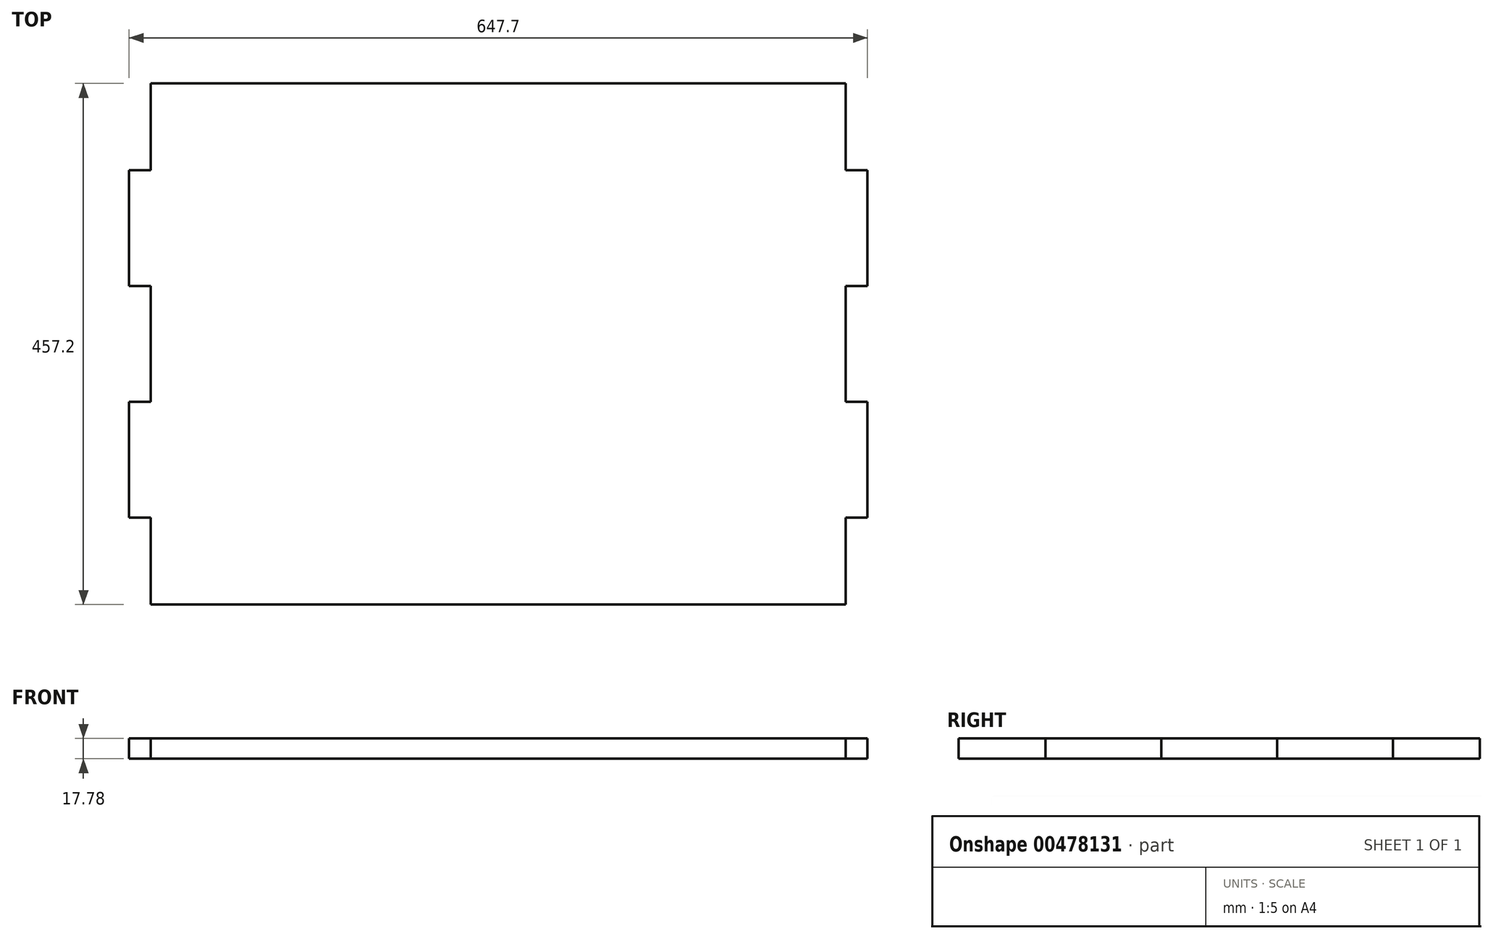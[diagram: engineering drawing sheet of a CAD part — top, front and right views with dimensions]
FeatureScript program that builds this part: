
annotation { "Feature Type Name" : "Feature", "Feature Type Description" : "" }
export const myFeature = defineFeature(function(context is Context, id is Id, definition is map)
    precondition{}
    {
        {
            var Q0;
            Q0=qCreatedBy(makeId("Top.planeOp"),FACE);
            var sketch = newSketch(context, id + "F0", { "sketchPlane" : qUnion([Q0])});
            skLineSegment(sketch, "E0.bottom", {"start": v(0, 0) * mm, "end": v(609.6, 0) * mm});
            skLineSegment(sketch, "E0.top", {"start": v(0, -457.2) * mm, "end": v(609.6, -457.2) * mm});
            skLineSegment(sketch, "E1.0", {"start": v(628.65, 0) * mm, "end": v(628.65, -457.2) * mm, "construction": true});
            skLineSegment(sketch, "E2.0", {"start": v(-19.05, 0) * mm, "end": v(-19.05, -457.2) * mm, "construction": true});
            skLineSegment(sketch, "E3.0", {"start": v(0, -76.2) * mm, "end": v(609.6, -76.2) * mm});
            skLineSegment(sketch, "E4.0", {"start": v(0, -381) * mm, "end": v(609.6, -381) * mm});
            skLineSegment(sketch, "E5.0", {"start": v(0, -279.4) * mm, "end": v(609.6, -279.4) * mm});
            skLineSegment(sketch, "E6.0", {"start": v(0, -177.8) * mm, "end": v(609.6, -177.8) * mm});
            skLineSegment(sketch, "E7", {"start": v(0, 0) * mm, "end": v(0, -76.2) * mm});
            skLineSegment(sketch, "E8", {"start": v(0, -177.8) * mm, "end": v(0, -76.2) * mm});
            skLineSegment(sketch, "E9", {"start": v(0, -177.8) * mm, "end": v(0, -279.4) * mm});
            skLineSegment(sketch, "E10", {"start": v(0, -279.4) * mm, "end": v(0, -381) * mm});
            skLineSegment(sketch, "E11", {"start": v(0, -457.2) * mm, "end": v(0, -381) * mm});
            skLineSegment(sketch, "E12", {"start": v(609.6, 0) * mm, "end": v(609.6, -76.2) * mm});
            skLineSegment(sketch, "E13", {"start": v(609.6, -177.8) * mm, "end": v(609.6, -76.2) * mm});
            skLineSegment(sketch, "E14", {"start": v(609.6, -177.8) * mm, "end": v(609.6, -279.4) * mm});
            skLineSegment(sketch, "E15", {"start": v(609.6, -279.4) * mm, "end": v(609.6, -381) * mm});
            skLineSegment(sketch, "E16", {"start": v(609.6, -457.2) * mm, "end": v(609.6, -381) * mm});
            skLineSegment(sketch, "E17.0", {"start": v(-19.05, -177.8) * mm, "end": v(-19.05, -76.2) * mm});
            skLineSegment(sketch, "E18.0", {"start": v(628.65, -177.8) * mm, "end": v(628.65, -76.2) * mm});
            skLineSegment(sketch, "E19.0", {"start": v(628.65, -279.4) * mm, "end": v(628.65, -381) * mm});
            skLineSegment(sketch, "E20.0", {"start": v(-19.05, -279.4) * mm, "end": v(-19.05, -381) * mm});
            skLineSegment(sketch, "E21", {"start": v(-19.05, -76.2) * mm, "end": v(0, -76.2) * mm});
            skLineSegment(sketch, "E22", {"start": v(0, -177.8) * mm, "end": v(-19.05, -177.8) * mm});
            skLineSegment(sketch, "E23", {"start": v(-19.05, -279.4) * mm, "end": v(0, -279.4) * mm});
            skLineSegment(sketch, "E24", {"start": v(0, -381) * mm, "end": v(-19.05, -381) * mm});
            skLineSegment(sketch, "E25", {"start": v(609.6, -381) * mm, "end": v(628.65, -381) * mm});
            skLineSegment(sketch, "E26", {"start": v(628.65, -279.4) * mm, "end": v(609.6, -279.4) * mm});
            skLineSegment(sketch, "E27", {"start": v(609.6, -76.2) * mm, "end": v(628.65, -76.2) * mm});
            skLineSegment(sketch, "E28", {"start": v(628.65, -177.8) * mm, "end": v(609.6, -177.8) * mm});
            skSolve(sketch);
        }
        {
            var Q0;
            Q0=makeQuery(id+"F0.imprint","IMPRINT",FACE,{"disambiguationData":[TD([[makeQuery(id+"F0.imprint","IMPRINT",EDGE,{"derivedFrom":sQuery(id+"F0.wireOp",EDGE,"E0.bottom")}),-1.0]])]});
            var Q1;
            Q1=makeQuery(id+"F0.imprint","IMPRINT",FACE,{"disambiguationData":[TD([[makeQuery(id+"F0.imprint","IMPRINT",EDGE,{"derivedFrom":sQuery(id+"F0.wireOp",EDGE,"E5.0")}),1.0]])]});
            var Q2;
            Q2=makeQuery(id+"F0.imprint","IMPRINT",FACE,{"disambiguationData":[TD([[makeQuery(id+"F0.imprint","IMPRINT",EDGE,{"derivedFrom":sQuery(id+"F0.wireOp",EDGE,"E4.0")}),1.0]])]});
            var Q3;
            Q3=makeQuery(id+"F0.imprint","IMPRINT",FACE,{"disambiguationData":[TD([[makeQuery(id+"F0.imprint","IMPRINT",EDGE,{"derivedFrom":sQuery(id+"F0.wireOp",EDGE,"E0.top")}),1.0]])]});
            var Q4;
            Q4=makeQuery(id+"F0.imprint","IMPRINT",FACE,{"disambiguationData":[TD([[makeQuery(id+"F0.imprint","IMPRINT",EDGE,{"derivedFrom":sQuery(id+"F0.wireOp",EDGE,"E10")}),-1.0]])]});
            var Q5;
            Q5=makeQuery(id+"F0.imprint","IMPRINT",FACE,{"disambiguationData":[TD([[makeQuery(id+"F0.imprint","IMPRINT",EDGE,{"derivedFrom":sQuery(id+"F0.wireOp",EDGE,"E8")}),1.0]])]});
            var Q6;
            Q6=makeQuery(id+"F0.imprint","IMPRINT",FACE,{"disambiguationData":[TD([[makeQuery(id+"F0.imprint","IMPRINT",EDGE,{"derivedFrom":sQuery(id+"F0.wireOp",EDGE,"E3.0")}),-1.0]])]});
            var Q7;
            Q7=makeQuery(id+"F0.imprint","IMPRINT",FACE,{"disambiguationData":[TD([[makeQuery(id+"F0.imprint","IMPRINT",EDGE,{"derivedFrom":sQuery(id+"F0.wireOp",EDGE,"E13")}),-1.0]])]});
            var Q8;
            Q8=makeQuery(id+"F0.imprint","IMPRINT",FACE,{"disambiguationData":[TD([[makeQuery(id+"F0.imprint","IMPRINT",EDGE,{"derivedFrom":sQuery(id+"F0.wireOp",EDGE,"E15")}),1.0]])]});
            extrude(context, id + "F1", {"entities" : qUnion([Q0, Q1, Q2, Q3, Q4, Q5, Q6, Q7, Q8]), "depth" : 17.78 * mm});
        }
    });
